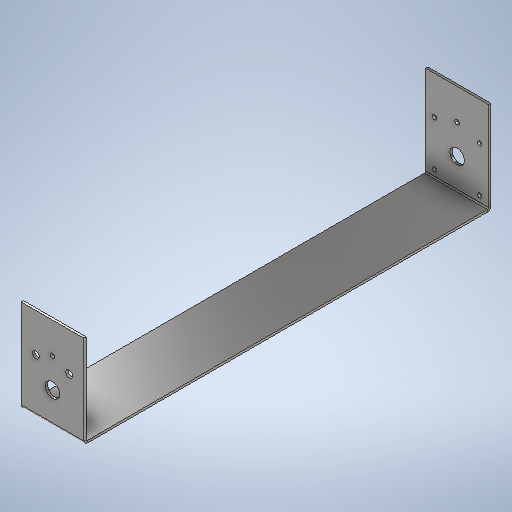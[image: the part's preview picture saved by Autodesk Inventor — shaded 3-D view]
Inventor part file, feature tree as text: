
AUTODESK INVENTOR PART (.ipt)
format: ipt  version: 2025.1 (Build 291241020, 241B)  size: 327,680 bytes
history: native  units: in
note: dims shown in document units (in); Inventor stores cm internally (conversion verified against a paired STEP export)
features: sheet_metal_op x7, sketch x7, hole x4, other x3
ambient origin geometry x8: Origin, YZ Plane, XZ Plane, XY Plane, X Axis, Y Axis, Z Axis, Center Point
bodies: Solid1 (feature_tree)
feature tree (21):
  sheet_metal_op  "Face1"
  sheet_metal_op  "Flange1"
  sheet_metal_op  "Flange2"
  hole  "Hole2"  [1 undecoded]
  hole  "Hole3"  [1 undecoded]
  hole  "Hole4"  [1 undecoded]
  hole  "Hole5"  [1 undecoded]
  sketch  "Sketch2"  dims[d2=1.7in d3=10.875in]
  other  "Plate1"
  sketch  "Sketch3"  dims[d4=0.0625in d5=0.0625in]
  other  "Plate2"
  sheet_metal_op  "Bend1"
  sheet_metal_op  "Corner1"
  sketch  "Sketch4"  dims[d6=0.0312in d7=0.125in]
  other  "Plate3"
  sheet_metal_op  "Bend2"
  sheet_metal_op  "Corner2"
  sketch  "Sketch5"  dims[d8=0.0625in d9=2.5in d10=90.0deg d11=0.03in]
  sketch  "Sketch7"  dims[d12=0.25in]
  sketch  "Sketch8"  dims[d13=0.0625in]
  sketch  "Sketch9"  dims[d14=0.0625in d15=0.0625in d16=0.0312in d17=0.125in d18=0.0625in d19=2.5in d20=90.0deg d21=0.03in d22=0.25in d23=0.0625in d24=0.0625in d37=0.8in d38=0.85in d39=0.85in d40=0.125in d41=0.75in d42=0.375in d43=0.25in d44=0.5635in d45=1.0in d46=0.8108in d47=0.398in d48=0.75in d49=0.375in d50=0.25in d51=0.5635in d52=1.0in d53=0.8108in d54=0.4in d55=0.4in d56=0.6in d57=0.6in d58=0.1875in d59=0.75in d60=0.375in d61=0.25in d62=0.5635in d63=1.0in d64=0.8108in d65=0.61in d68=0.61in d69=0.61in d70=0.61in d71=0.61in d72=0.61in d73=0.61in d74=0.61in d75=0.125in d76=0.75in d77=0.375in d78=0.25in d79=0.5635in d80=1.0in d81=0.8108in d83=0.8in d29=1.0in d30=1.0in d31=1.0in d32=0.15in d33=0.25in d34=0.375in d35=0.5635in d36=0.75in]
note: 4 required parameter values undecoded (feature->parameter linkage not recoverable at this tier; creation-order binding heuristic only, values carry confidence <= 0.55)
